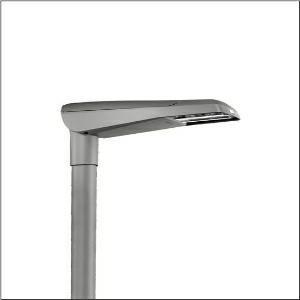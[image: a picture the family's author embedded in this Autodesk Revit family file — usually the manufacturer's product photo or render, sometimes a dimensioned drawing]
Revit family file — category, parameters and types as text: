
# Revit family: streetlight_sl_11_iq_micro___p1_0a_5xc1c41f08ce_dca2
name_source: partatom
category: Lighting Fixtures
units: mm (PartAtom-declared; Revit-internal decimal feet)

## family parameters
Cut with Voids When Loaded = No
Host = Face
Light Source = No
Part Type = Normal
Room Calculation Point = No
Round Connector Dimension = Use Diameter
Shared = No

## types (1)
- --- (1 x LED, 1660 lm, 10.8 W, 4000K)
    Apparent Load = 11 VA
    CIE Flux Codes = 29 63 93 100 100
    Color Rendering = 70
    Color Temperature = 4000K
    Default Elevation = 1800 mm
    Description = Streetlight SL 11 iQ micro, mast luminaire, primary light control with 3 zone facetted reflector, of plastic, silver coated, highly specular, primary optical cover: cover, of PMMA, transparent, light distribution: P1.0a, light emission: direct distribution, primary light characteristic: asymmetric, installation type: post-top, side-entry, lamps: LED, High Power LED, rated values: 1.660lm | 10,8W | 153,7lm/W (begin service life); end service life: 1.660lm | 11,1W; at 50% lumin. flux: 830lm | 6W | 138,3lm/W, colour temperature: 4000K, colour rendering: CRI > 70, light colour: 740, light setting 1 begin service life: 100% | 1.660lm | 10,8W | 153,7lm/W | 4.000K, light setting 1 end service life: 11,1W, further light settings possible, control: Street-Remote, optimised constant luminous flux control (CLO 2.0), Desk-Remote (wireless, voltage-free reading and setting of iQ features in the workshop via application-optimized NFC function/RFID function), Light-Fading, Smart-Wire, Night-Set, Lumen-Switch, Temp-Guard, Auto-Match, with cable H07RN-F 3x 1.5mm², mains connection: 230..240V, AC, 50/60Hz, connection cable pre-assembled, cable length: 5,5m, luminaire housing, of diecast aluminium, powder-coated, SITECO metallic grey (DB 702S), please order mast flange separately, inclination adjustable without tools: 0°, 5°, 10°, 15° (post-top) | 0°, -5°, -10°, -15° (side-entry), sealing non-destructively replaceable, multi-level sealing system, length: 600mm, width: 174mm, height: 116mm, mast flange for spigot size: 42mm (side-entry): 5XC10008XM4, 60/48mm (side-entry/post-top): 5XC10108XM2, 76/60mm (side-entry/post-top): 5XC10108XM1, equipment: standard, protection rating (complete): IP66, insulation class (complete): insulation class II (safety insulation), certification: CE, ENEC, ENEC+, VDE, impact resistance: IK10, permissible operating ambient temperature for outdoor applications: -25..+50°C, standard-compliant lighting for roads and squares, Environmental Product Declaration (EPD) tested and certified by an independent institute, packaging unit: 1 piece

Light Distribution: P1.0a
    Height = 116 mm
    Lamp = 1 x LED
    Lamp Light Flux = 1660 lm
    Lamp Power = 10.8 W
    Lamp count = 1
    Length = 600 mm
    Luminous efficacy = 154 lm/W
    Manufacturer = Siteco
    ModVariant = No
    Model = 5XC1C41F08CE
    Number of Poles = 1
    OnlyDefault = Yes
    Power Factor = 1
    Product Name = Streetlight SL 11 iQ micro | P1.0a
    Product group = mast luminaire | pylon top
    ProductGroupID = 6100
    Protection Class = Protection class II
    Protection Degree = IP 66
    RLX_Detail_Level = 1
    RLX_Emergency_Light_Flux = 0 lm
    RLX_Emergency_Type = 0
    RLX_Emergency_Type_DB = No
    RlxData = <blob elided: 26633 chars, md5=55373fbb>
    Socket = socket
    Standby Power = 0 W
    System Light Flux = 1660 lm
    System Power = 11 W
    Type Comments = factory setting: luminous flux: 100 % | dim-lin: 254 | 194 mA
    Type Image = l_1006566.jpg
    URL = http://relux.com
    VarID = @adj_019307
    Voltage = 0 V
    Weight = 0.00 kg
    Width = 174 mm

## geometry (parser evidence)
native form markers: Blend x4, Sweep x12
no freeform markers — native parametric forms only
